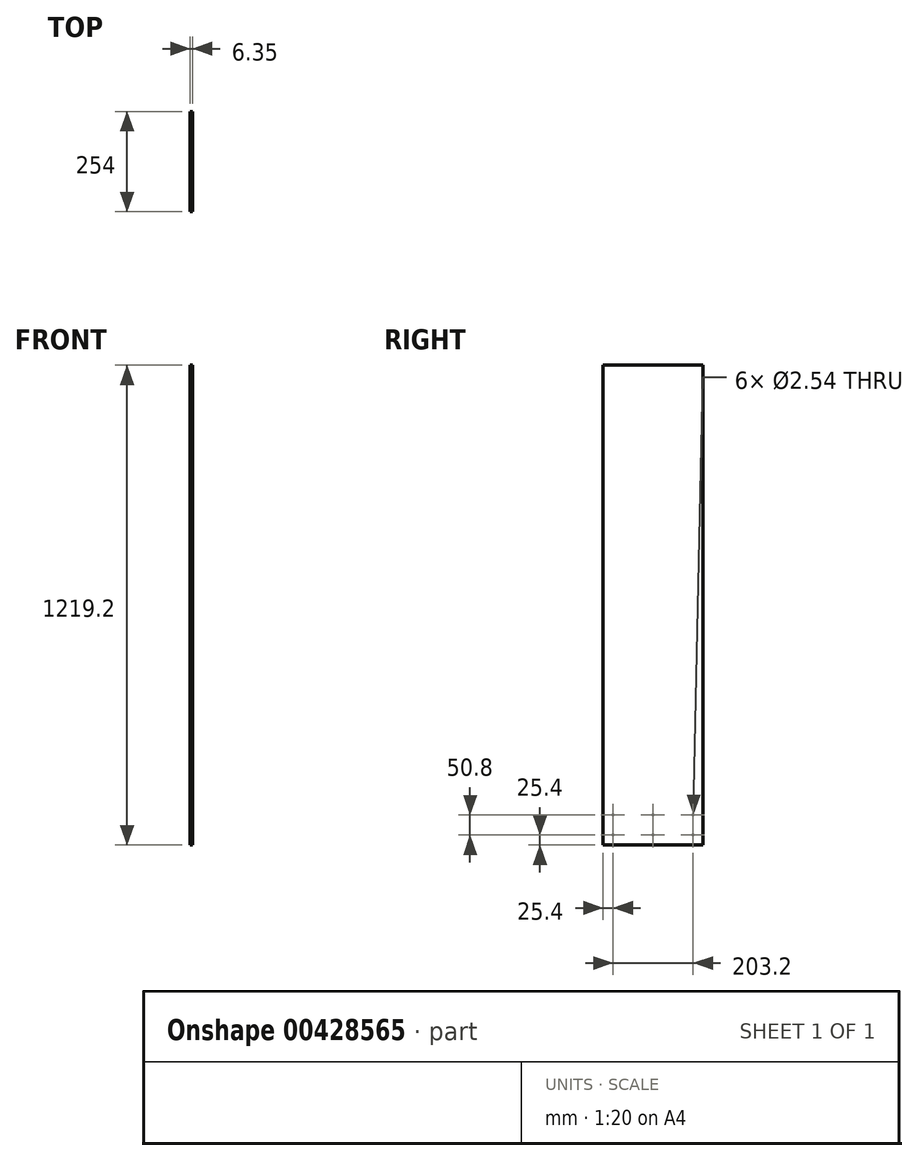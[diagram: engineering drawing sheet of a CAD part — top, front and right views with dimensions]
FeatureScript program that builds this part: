
annotation { "Feature Type Name" : "Feature", "Feature Type Description" : "" }
export const myFeature = defineFeature(function(context is Context, id is Id, definition is map)
    precondition{}
    {
        {
            var Q0;
            Q0=qCreatedBy(makeId("Right.planeOp"),FACE);
            var sketch = newSketch(context, id + "F0", { "sketchPlane" : qUnion([Q0])});
            skLineSegment(sketch, "E0.bottom", {"start": v(-127, -609.6) * mm, "end": v(127, -609.6) * mm});
            skLineSegment(sketch, "E0.top", {"start": v(-127, 609.6) * mm, "end": v(127, 609.6) * mm});
            skLineSegment(sketch, "E0.left", {"start": v(-127, -609.6) * mm, "end": v(-127, 609.6) * mm});
            skLineSegment(sketch, "E0.right", {"start": v(127, -609.6) * mm, "end": v(127, 609.6) * mm});
            skPoint(sketch, "E0.middle", {"position": v(0, 0) * mm});
            skLineSegment(sketch, "E1.top", {"start": v(-127, -508) * mm, "end": v(127, -508) * mm});
            skLineSegment(sketch, "E1.left", {"start": v(-127, -609.6) * mm, "end": v(-127, -508) * mm});
            skLineSegment(sketch, "E1.right", {"start": v(127, -609.6) * mm, "end": v(127, -508) * mm});
            skCircle(sketch, "E2", {"center": v(-101.6, -533.4) * mm, "radius": 1.27 * mm});
            skCircle(sketch, "E3", {"center": v(-101.6, -584.2) * mm, "radius": 1.27 * mm});
            skCircle(sketch, "E4", {"center": v(0, -533.4) * mm, "radius": 1.27 * mm});
            skCircle(sketch, "E5", {"center": v(0, -584.2) * mm, "radius": 1.27 * mm});
            skCircle(sketch, "E6", {"center": v(101.6, -533.4) * mm, "radius": 1.27 * mm});
            skCircle(sketch, "E7", {"center": v(101.6, -584.2) * mm, "radius": 1.27 * mm});
            skSolve(sketch);
        }
        {
            var Q0;
            Q0=makeQuery(id+"F0.imprint","IMPRINT",FACE,{"disambiguationData":[TD([[makeQuery(id+"F0.imprint","IMPRINT",EDGE,{"derivedFrom":sQuery(id+"F0.wireOp",EDGE,"E0.top")}),-1.0]])]});
            var Q1;
            Q1=makeQuery(id+"F0.imprint","IMPRINT",FACE,{"disambiguationData":[TD([[makeQuery(id+"F0.imprint","IMPRINT",EDGE,{"derivedFrom":sQuery(id+"F0.wireOp",EDGE,"E0.bottom")}),1.0]])]});
            extrude(context, id + "F1", {"entities" : qUnion([Q0, Q1]), "depth" : 6.35 * mm});
        }
    });
